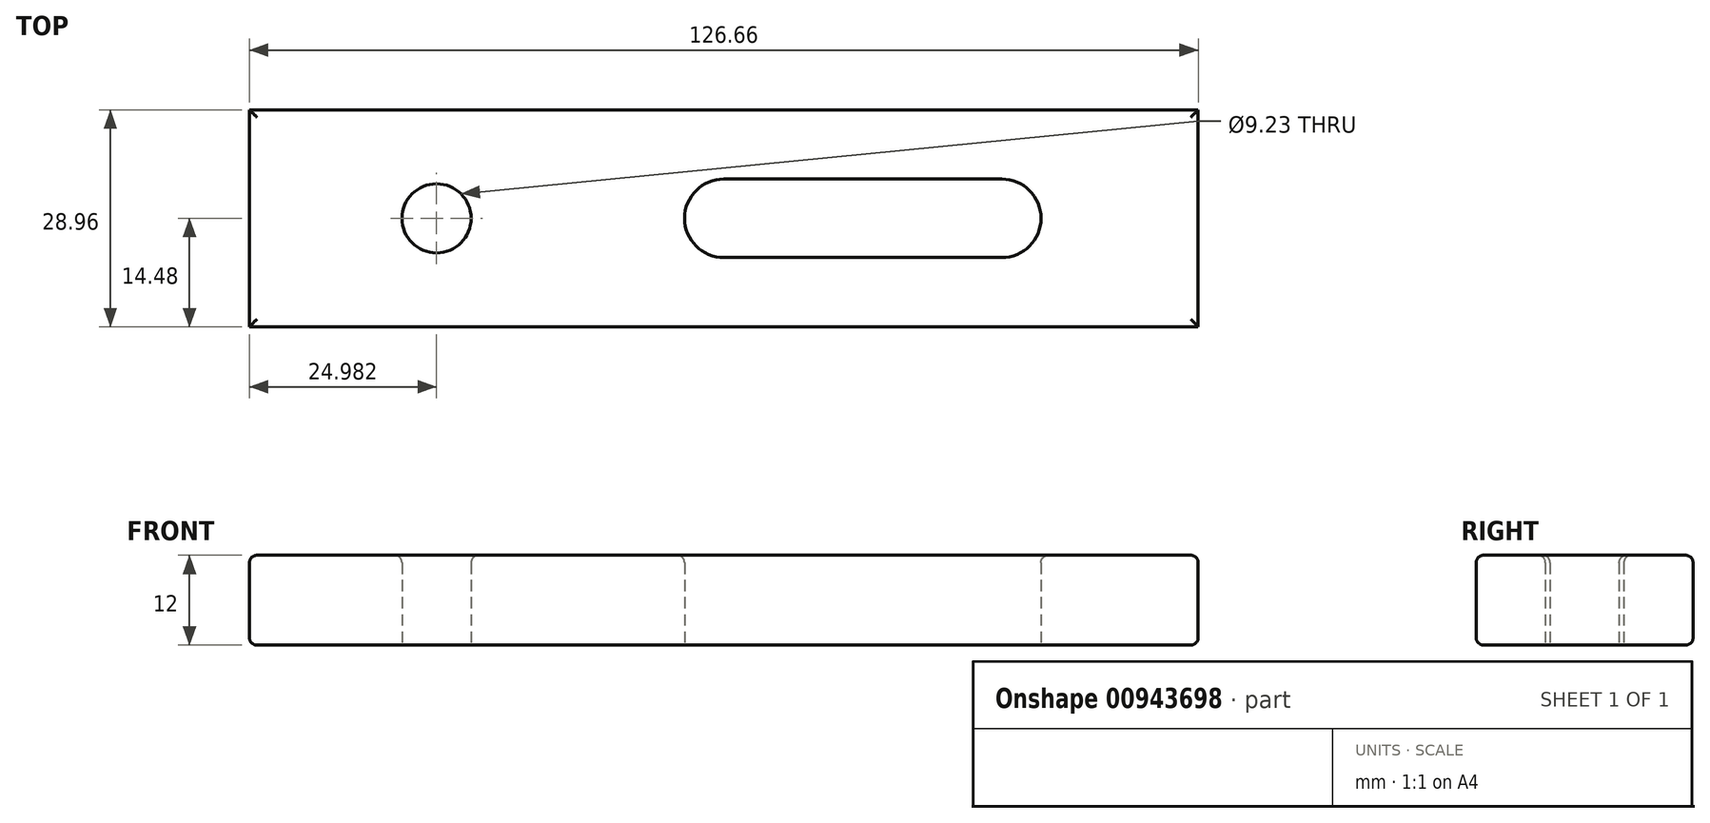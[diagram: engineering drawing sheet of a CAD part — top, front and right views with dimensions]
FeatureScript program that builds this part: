
annotation { "Feature Type Name" : "Feature", "Feature Type Description" : "" }
export const myFeature = defineFeature(function(context is Context, id is Id, definition is map)
    precondition{}
    {
        {
            var Q0;
            Q0=qCreatedBy(makeId("Top.planeOp"),FACE);
            var sketch = newSketch(context, id + "F0", { "sketchPlane" : qUnion([Q0])});
            skLineSegment(sketch, "E0.bottom", {"start": v(63.33, -14.48) * mm, "end": v(-63.33, -14.48) * mm});
            skLineSegment(sketch, "E0.top", {"start": v(63.33, 14.48) * mm, "end": v(-63.33, 14.48) * mm});
            skLineSegment(sketch, "E0.left", {"start": v(63.33, -14.48) * mm, "end": v(63.33, 14.48) * mm});
            skLineSegment(sketch, "E0.right", {"start": v(-63.33, -14.48) * mm, "end": v(-63.33, 14.48) * mm});
            skPoint(sketch, "E0.middle", {"position": v(0, 0) * mm});
            skArc(sketch, "E1", {"start": v(0, 5.24) * mm, "mid": v(-5.24, 0) * mm, "end": v(0, -5.24) * mm});
            skLineSegment(sketch, "E2.bottom", {"start": v(0, -5.24) * mm, "end": v(37.1, -5.24) * mm});
            skLineSegment(sketch, "E2.top", {"start": v(0, 5.24) * mm, "end": v(37.1, 5.24) * mm});
            skPoint(sketch, "E2.middle", {"position": v(18.55, 0) * mm});
            skArc(sketch, "E3", {"start": v(37.1, -5.24) * mm, "mid": v(42.34, 0) * mm, "end": v(37.1, 5.24) * mm});
            skCircle(sketch, "E4", {"center": v(-38.35, 0) * mm, "radius": 4.61 * mm});
            skSolve(sketch);
        }
        {
            var Q0;
            Q0=makeQuery(id+"F0.imprint","IMPRINT",FACE,{"disambiguationData":[TD([[makeQuery(id+"F0.imprint","IMPRINT",EDGE,{"derivedFrom":sQuery(id+"F0.wireOp",EDGE,"E0.bottom")}),-1.0]])]});
            extrude(context, id + "F1", {"entities" : qUnion([Q0]), "depth" : 12 * mm, "offsetDistance" : 25 * mm});
        }
        {
            var Q0;
            Q0=makeQuery(id+"F1.opExtrude","CAP_EDGE",EDGE,{"disambiguationData":[OSD([sQuery(id+"F0.wireOp",EDGE,"E4")])],"isStart":false});
            var Q1;
            Q1=makeQuery(id+"F1.opExtrude","CAP_EDGE",EDGE,{"disambiguationData":[OSD([sQuery(id+"F0.wireOp",EDGE,"E3")])],"isStart":false});
            fillet(context, id + "F2", {"entities" : qUnion([Q0, Q1]), "radius" : 1 * mm, "tangentPropagation" : true, "allowEdgeOverflow" : false});
        }
        {
            var Q0;
            Q0=makeQuery(id+"F1.opExtrude","CAP_EDGE",EDGE,{"disambiguationData":[OSD([sQuery(id+"F0.wireOp",EDGE,"E0.bottom")])],"isStart":true});
            var Q1;
            Q1=makeQuery(id+"F1.opExtrude","CAP_EDGE",EDGE,{"disambiguationData":[OSD([sQuery(id+"F0.wireOp",EDGE,"E0.top")])],"isStart":true});
            var Q2;
            Q2=makeQuery(id+"F1.opExtrude","CAP_EDGE",EDGE,{"disambiguationData":[OSD([sQuery(id+"F0.wireOp",EDGE,"E0.left")])],"isStart":true});
            var Q3;
            Q3=makeQuery(id+"F1.opExtrude","CAP_EDGE",EDGE,{"disambiguationData":[OSD([sQuery(id+"F0.wireOp",EDGE,"E0.right")])],"isStart":true});
            fillet(context, id + "F3", {"entities" : qUnion([Q0, Q1, Q2, Q3]), "radius" : 1 * mm, "tangentPropagation" : true, "allowEdgeOverflow" : false});
        }
        {
            var Q0;
            Q0=makeQuery(id+"F1.opExtrude","CAP_EDGE",EDGE,{"disambiguationData":[OSD([sQuery(id+"F0.wireOp",EDGE,"E0.bottom")])],"isStart":false});
            var Q1;
            Q1=makeQuery(id+"F1.opExtrude","CAP_EDGE",EDGE,{"disambiguationData":[OSD([sQuery(id+"F0.wireOp",EDGE,"E0.left")])],"isStart":false});
            var Q2;
            Q2=makeQuery(id+"F1.opExtrude","CAP_EDGE",EDGE,{"disambiguationData":[OSD([sQuery(id+"F0.wireOp",EDGE,"E0.top")])],"isStart":false});
            var Q3;
            Q3=makeQuery(id+"F1.opExtrude","CAP_EDGE",EDGE,{"disambiguationData":[OSD([sQuery(id+"F0.wireOp",EDGE,"E0.right")])],"isStart":false});
            fillet(context, id + "F4", {"entities" : qUnion([Q0, Q1, Q2, Q3]), "radius" : 1 * mm, "tangentPropagation" : true, "allowEdgeOverflow" : false});
        }
    });
